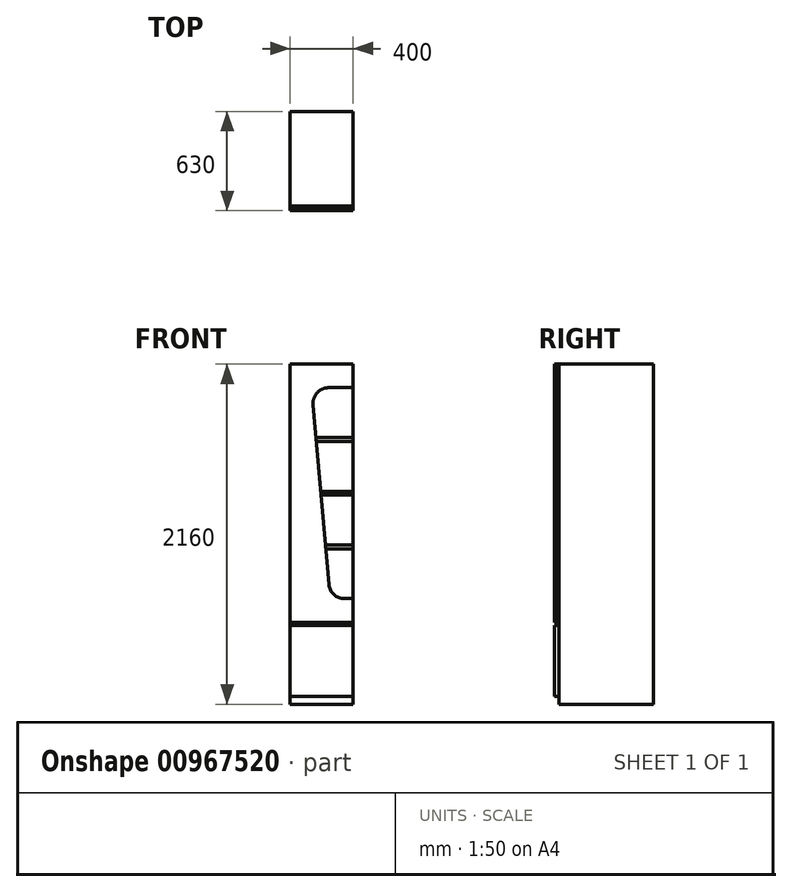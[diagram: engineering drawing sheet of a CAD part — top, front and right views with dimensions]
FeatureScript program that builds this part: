
annotation { "Feature Type Name" : "Feature", "Feature Type Description" : "" }
export const myFeature = defineFeature(function(context is Context, id is Id, definition is map)
    precondition{}
    {
        {
            assignVariable(context, id + "F0", {"variableType" : VariableType.LENGTH, "name" : "H", "lengthValue" : 2200 * mm});
        }
        {
            var Q0;
            Q0=qCreatedBy(makeId("Top.planeOp"),FACE);
            var sketch = newSketch(context, id + "F1", { "sketchPlane" : qUnion([Q0])});
            skLineSegment(sketch, "E0.bottom", {"start": v(0, 0) * mm, "end": v(400, 0) * mm});
            skLineSegment(sketch, "E0.top", {"start": v(0, 600) * mm, "end": v(400, 600) * mm});
            skLineSegment(sketch, "E0.left", {"start": v(0, 0) * mm, "end": v(0, 600) * mm});
            skLineSegment(sketch, "E0.right", {"start": v(400, 0) * mm, "end": v(400, 600) * mm});
            skSolve(sketch);
        }
        {
            var Q0;
            Q0 = qSketchRegion(id + "F1", true);
            extrude(context, id + "F2", {"entities" : qUnion([Q0]), "depth" : getVariable(context, 'H') - 40 * mm, "offsetDistance" : 25 * mm});
        }
        {
            var Q0;
            Q0=makeQuery(id+"F2.opExtrude","SWEPT_FACE",FACE,{"disambiguationData":[OSD([sQuery(id+"F1.wireOp",EDGE,"E0.bottom")])]});
            var sketch = newSketch(context, id + "F3", { "sketchPlane" : qUnion([Q0])});
            skLineSegment(sketch, "E1.bottom", {"start": v(0, 500) * mm, "end": v(400, 500) * mm});
            skLineSegment(sketch, "E1.top", {"start": v(0, 50) * mm, "end": v(400, 50) * mm});
            skLineSegment(sketch, "E1.left", {"start": v(0, 500) * mm, "end": v(0, 50) * mm});
            skLineSegment(sketch, "E1.right", {"start": v(400, 500) * mm, "end": v(400, 50) * mm});
            skLineSegment(sketch, "E2.bottom", {"start": v(0, 2160) * mm, "end": v(400, 2160) * mm});
            skLineSegment(sketch, "E2.top", {"start": v(0, 520) * mm, "end": v(400, 520) * mm});
            skLineSegment(sketch, "E2.left", {"start": v(0, 2160) * mm, "end": v(0, 520) * mm});
            skLineSegment(sketch, "E2.right", {"start": v(400, 2160) * mm, "end": v(400, 520) * mm});
            skLineSegment(sketch, "E3", {"start": v(200, 2160) * mm, "end": v(200, 50) * mm, "construction": true});
            skLineSegment(sketch, "E4.MirrorCS", {"start": v(400, 1693.75) * mm, "end": v(400, 1668.75) * mm, "construction": true});
            skLineSegment(sketch, "E5.MirrorCS", {"start": v(400, 1011.25) * mm, "end": v(400, 986.25) * mm, "construction": true});
            skLineSegment(sketch, "E6.MirrorCS", {"start": v(400, 1352.5) * mm, "end": v(400, 1327.5) * mm, "construction": true});
            skArc(sketch, "E7.MirrorCS", {"start": v(344.87, 670) * mm, "mid": v(277.3, 696.27) * mm, "end": v(245.25, 761.28) * mm});
            skLineSegment(sketch, "E8.MirrorCS", {"start": v(400, 2010) * mm, "end": v(245.13, 2010) * mm});
            skLineSegment(sketch, "E9.MirrorCS", {"start": v(344.87, 670) * mm, "end": v(400, 670) * mm});
            skLineSegment(sketch, "E10.MirrorCS", {"start": v(400, 986.25) * mm, "end": v(225.57, 986.25) * mm});
            skLineSegment(sketch, "E11.MirrorCS", {"start": v(400, 986.25) * mm, "end": v(400, 670) * mm, "construction": true});
            skLineSegment(sketch, "E12.MirrorCS", {"start": v(400, 1011.25) * mm, "end": v(223.38, 1011.25) * mm});
            skLineSegment(sketch, "E13.MirrorCS", {"start": v(400, 1327.5) * mm, "end": v(195.71, 1327.5) * mm});
            skLineSegment(sketch, "E14.MirrorCS", {"start": v(400, 2010) * mm, "end": v(400, 1693.75) * mm, "construction": true});
            skLineSegment(sketch, "E15.MirrorCS", {"start": v(400, 1327.5) * mm, "end": v(400, 1011.25) * mm, "construction": true});
            skLineSegment(sketch, "E16.MirrorCS", {"start": v(400, 1693.75) * mm, "end": v(163.67, 1693.75) * mm});
            skLineSegment(sketch, "E17.MirrorCS", {"start": v(145.51, 1901.28) * mm, "end": v(245.25, 761.28) * mm});
            skArc(sketch, "E18.MirrorCS", {"start": v(145.51, 1901.28) * mm, "mid": v(171.4, 1977.56) * mm, "end": v(245.13, 2010) * mm});
            skLineSegment(sketch, "E19.MirrorCS", {"start": v(400, 1668.75) * mm, "end": v(400, 1352.5) * mm, "construction": true});
            skLineSegment(sketch, "E20.MirrorCS", {"start": v(400, 1668.75) * mm, "end": v(165.86, 1668.75) * mm});
            skLineSegment(sketch, "E21.MirrorCS", {"start": v(400, 1352.5) * mm, "end": v(193.52, 1352.5) * mm});
            skPoint(sketch, "E22", {"position": v(136, 2010) * mm});
            skSolve(sketch);
        }
        {
            var Q0;
            Q0=makeQuery(id+"F3.imprint","IMPRINT",FACE,{"disambiguationData":[TD([[makeQuery(id+"F3.imprint","IMPRINT",EDGE,{"derivedFrom":sQuery(id+"F3.wireOp",EDGE,"E1.bottom")}),-1.0]])]});
            var Q1;
            {var subQ5=sQuery(id+"F3.wireOp",EDGE,"E2.bottom");Q1=makeQuery(id+"F3.imprint","IMPRINT",FACE,{"disambiguationData":[TD([[makeQuery(id+"F3.imprint","IMPRINT",EDGE,{"derivedFrom":subQ5}),-1.0]])]});}
            extrude(context, id + "F4", {"entities" : qUnion([Q0, Q1]), "depth" : 30 * mm, "offsetDistance" : 25 * mm});
        }
        {
            var Q0;
            {var subQ1=sQuery(id+"F3.wireOp",EDGE,"E8.MirrorCS");Q0=makeQuery(id+"F3.imprint","IMPRINT",FACE,{"disambiguationData":[TD([[makeQuery(id+"F3.imprint","IMPRINT",EDGE,{"derivedFrom":subQ1}),1.0]])]});}
            var Q1;
            {var subQ0=sQuery(id+"F3.wireOp",EDGE,"E20.MirrorCS");Q1=makeQuery(id+"F3.imprint","IMPRINT",FACE,{"disambiguationData":[TD([[makeQuery(id+"F3.imprint","IMPRINT",EDGE,{"derivedFrom":subQ0}),1.0]])]});}
            var Q2;
            {var subQ0=sQuery(id+"F3.wireOp",EDGE,"E12.MirrorCS");Q2=makeQuery(id+"F3.imprint","IMPRINT",FACE,{"disambiguationData":[TD([[makeQuery(id+"F3.imprint","IMPRINT",EDGE,{"derivedFrom":subQ0}),-1.0]])]});}
            var Q3;
            {var subQ2=sQuery(id+"F3.wireOp",EDGE,"E7.MirrorCS");Q3=makeQuery(id+"F3.imprint","IMPRINT",FACE,{"disambiguationData":[TD([[makeQuery(id+"F3.imprint","IMPRINT",EDGE,{"derivedFrom":subQ2}),-1.0]])]});}
            extrude(context, id + "F5", {"entities" : qUnion([Q0, Q1, Q2, Q3]), "depth" : 10 * mm, "offsetDistance" : 25 * mm});
        }
        {
            var Q0;
            {var subQ0=sQuery(id+"F3.wireOp",EDGE,"E16.MirrorCS");Q0=makeQuery(id+"F3.imprint","IMPRINT",FACE,{"disambiguationData":[TD([[makeQuery(id+"F3.imprint","IMPRINT",EDGE,{"derivedFrom":subQ0}),1.0]])]});}
            var Q1;
            {var subQ0=sQuery(id+"F3.wireOp",EDGE,"E13.MirrorCS");Q1=makeQuery(id+"F3.imprint","IMPRINT",FACE,{"disambiguationData":[TD([[makeQuery(id+"F3.imprint","IMPRINT",EDGE,{"derivedFrom":subQ0}),-1.0]])]});}
            var Q2;
            {var subQ0=sQuery(id+"F3.wireOp",EDGE,"E10.MirrorCS");Q2=makeQuery(id+"F3.imprint","IMPRINT",FACE,{"disambiguationData":[TD([[makeQuery(id+"F3.imprint","IMPRINT",EDGE,{"derivedFrom":subQ0}),-1.0]])]});}
            extrude(context, id + "F6", {"entities" : qUnion([Q0, Q1, Q2]), "depth" : 10 * mm, "offsetDistance" : 25 * mm});
        }
    });
